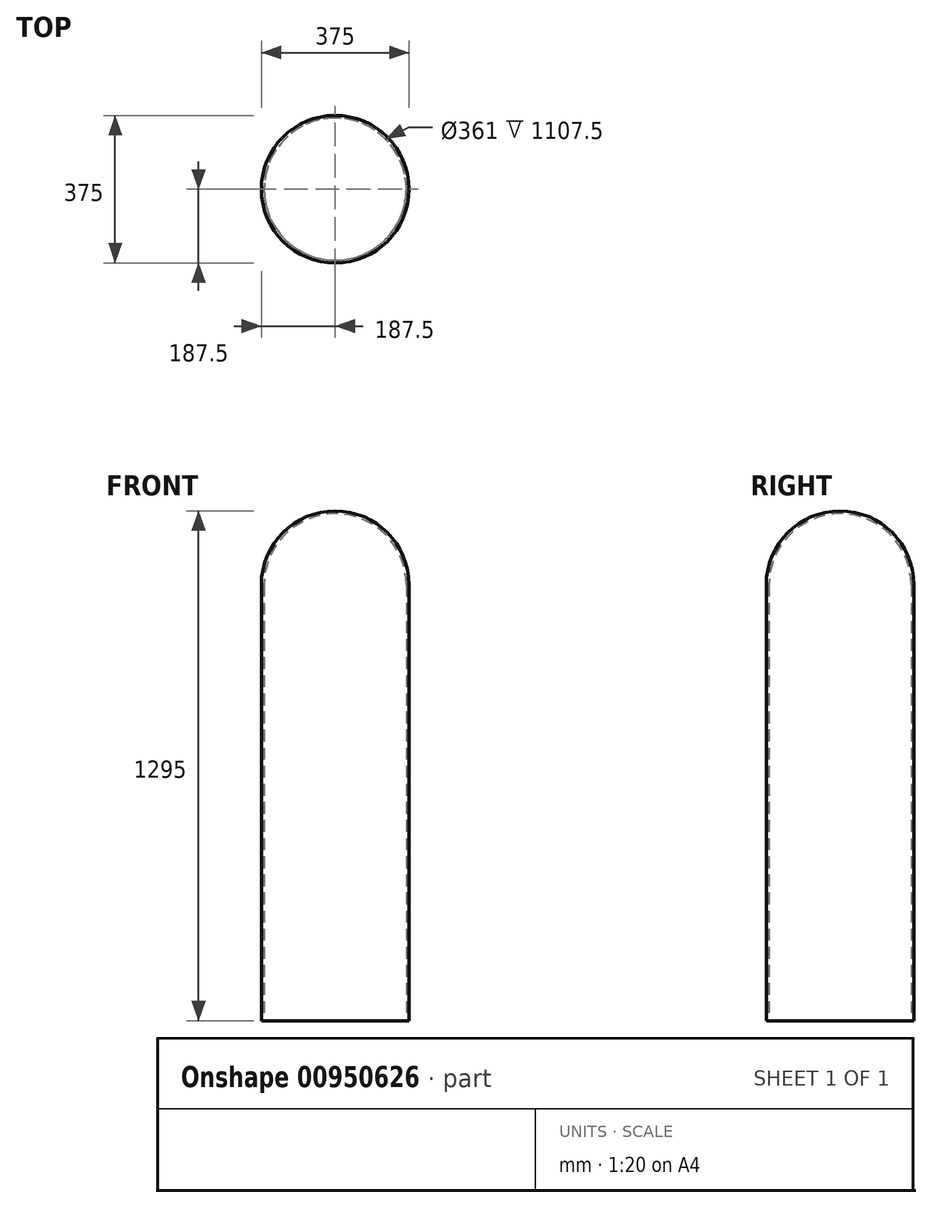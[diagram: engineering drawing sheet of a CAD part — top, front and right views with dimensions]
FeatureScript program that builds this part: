
annotation { "Feature Type Name" : "Feature", "Feature Type Description" : "" }
export const myFeature = defineFeature(function(context is Context, id is Id, definition is map)
    precondition{}
    {
        {
            var Q0;
            Q0=qCreatedBy(makeId("Top.planeOp"),FACE);
            var sketch = newSketch(context, id + "F0", { "sketchPlane" : qUnion([Q0])});
            skCircle(sketch, "E0", {"center": v(0, 0) * mm, "radius": 187.5 * mm});
            skSolve(sketch);
        }
        {
            var Q0;
            Q0=makeQuery(id+"F0.imprint","IMPRINT",FACE,{"disambiguationData":[TD([[makeQuery(id+"F0.imprint","IMPRINT",EDGE,{"derivedFrom":sQuery(id+"F0.wireOp",EDGE,"E0")}),1.0]])]});
            extrude(context, id + "F1", {"entities" : qUnion([Q0]), "depth" : 1102.5 * mm, "offsetDistance" : 25 * mm});
        }
        {
            var Q0;
            Q0=makeQuery(id+"F1.opExtrude","CAP_FACE",FACE,{"disambiguationData":[OSD([sQuery(id+"F0.wireOp",EDGE,"E0")])],"isStart":false});
            var sketch = newSketch(context, id + "F2", { "sketchPlane" : qUnion([Q0])});
            skCircle(sketch, "E1.0", {"center": v(0, 0) * mm, "radius": 187.5 * mm});
            skLineSegment(sketch, "E2", {"start": v(0, 0) * mm, "end": v(0, -187.5) * mm});
            skLineSegment(sketch, "E3", {"start": v(0, -187.5) * mm, "end": v(0, 187.5) * mm});
            skArc(sketch, "E4", {"start": v(0, 180.5) * mm, "mid": v(-180.5, 0) * mm, "end": v(0, -180.5) * mm});
            skSolve(sketch);
        }
        {
            var Q0;
            {var subQ4=sQuery(id+"F2.wireOp",EDGE,"E4");Q0=makeQuery(id+"F2.imprint","IMPRINT",FACE,{"disambiguationData":[TD([[makeQuery(id+"F2.imprint","IMPRINT",EDGE,{"derivedFrom":subQ4}),-1.0]])]});}
            var Q1;
            Q1=sQuery(id+"F2.wireOp",EDGE,"E2");
            revolve(context, id + "F3", {"operationType" : NewBodyOperationType.ADD, "surfaceOperationType" : NewSurfaceOperationType.NEW, "entities" : qUnion([Q0]), "axis" : qUnion([Q1]), "revolveType" : RevolveType.FULL});
        }
        {
            var Q0;
            Q0=makeQuery(id+"F1.opExtrude","CAP_FACE",FACE,{"disambiguationData":[OSD([sQuery(id+"F0.wireOp",EDGE,"E0")])],"isStart":true});
            var sketch = newSketch(context, id + "F4", { "sketchPlane" : qUnion([Q0])});
            skCircle(sketch, "E5", {"center": v(0, 0) * mm, "radius": 180.5 * mm});
            skSolve(sketch);
        }
        {
            var Q0;
            Q0 = qSketchRegion(id + "F4", true);
            extrude(context, id + "F5", {"entities" : qUnion([Q0]), "operationType" : NewBodyOperationType.REMOVE, "oppositeDirection" : true, "depth" : 1102.5 * mm, "offsetDistance" : 25 * mm});
        }
        {
            var Q0;
            Q0=makeQuery(id+"F1.opExtrude","CAP_FACE",FACE,{"disambiguationData":[OSD([sQuery(id+"F0.wireOp",EDGE,"E0")])],"isStart":true});
            var sketch = newSketch(context, id + "F6", { "sketchPlane" : qUnion([Q0])});
            skCircle(sketch, "E6.0", {"center": v(0, 0) * mm, "radius": 187.5 * mm});
            skSolve(sketch);
        }
        {
            var Q0;
            Q0=makeQuery(id+"F6.imprint","IMPRINT",FACE,{"disambiguationData":[TD([[makeQuery(id+"F6.imprint","IMPRINT",EDGE,{"derivedFrom":sQuery(id+"F6.wireOp",EDGE,"E6.0")}),-1.0]])]});
            var Q1;
            Q1=makeQuery(id+"F6.imprint","IMPRINT",FACE,{"disambiguationData":[TD([[makeQuery(id+"F6.imprint","IMPRINT",EDGE,{"derivedFrom":makeQuery(id+"F5.boolean.opBoolean","COPY",EDGE,{"derivedFrom":makeQuery(id+"F5.opExtrude","CAP_EDGE",EDGE,{"disambiguationData":[OSD([sQuery(id+"F4.wireOp",EDGE,"E5")])],"isStart":true})})}),1.0]])]});
            extrude(context, id + "F7", {"entities" : qUnion([Q0, Q1]), "operationType" : NewBodyOperationType.ADD, "depth" : 5 * mm, "offsetDistance" : 25 * mm});
        }
    });
